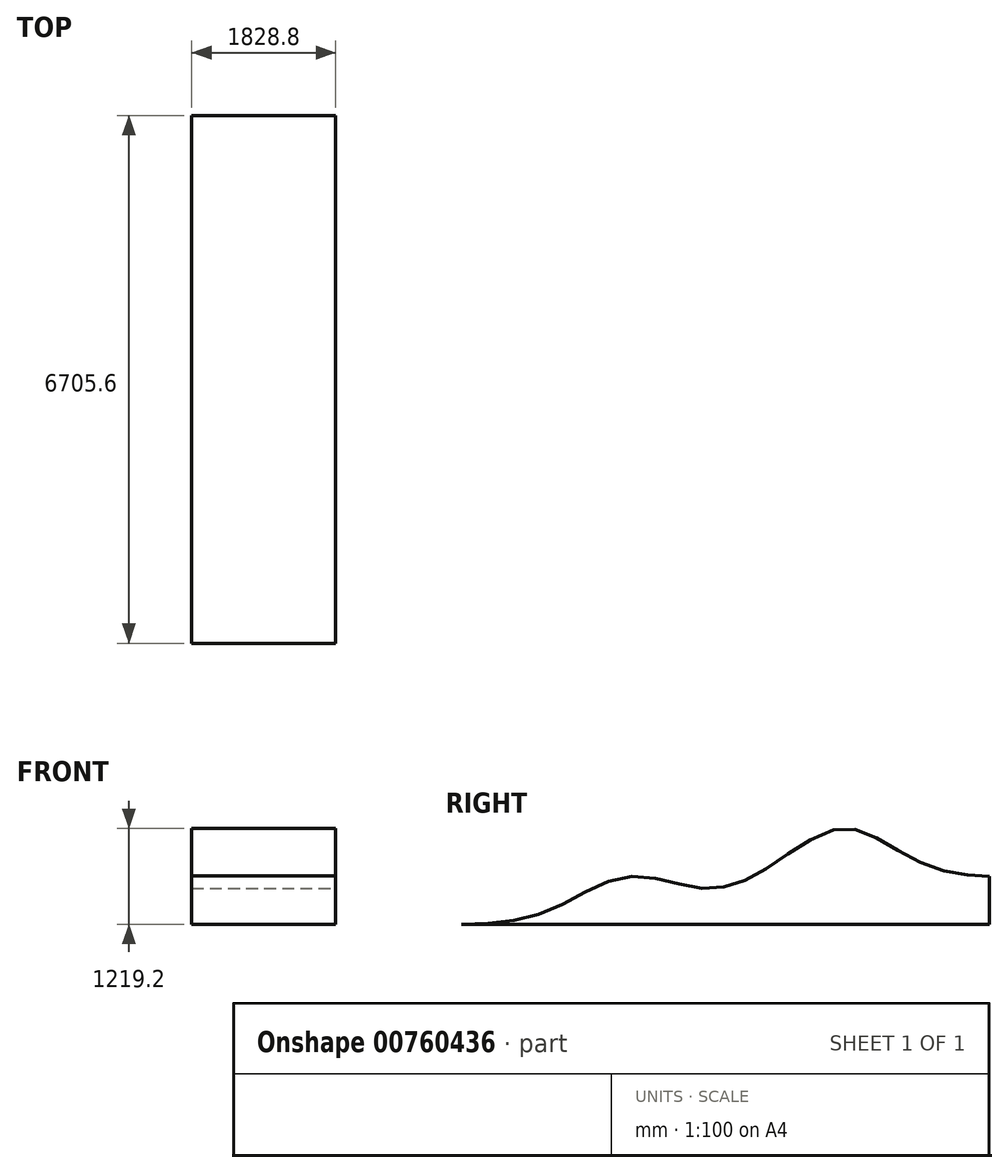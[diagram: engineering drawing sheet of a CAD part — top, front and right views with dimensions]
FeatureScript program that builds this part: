
annotation { "Feature Type Name" : "Feature", "Feature Type Description" : "" }
export const myFeature = defineFeature(function(context is Context, id is Id, definition is map)
    precondition{}
    {
        {
            var Q0;
            Q0=qCreatedBy(makeId("Right.planeOp"),FACE);
            var sketch = newSketch(context, id + "F0", { "sketchPlane" : qUnion([Q0])});
            skLineSegment(sketch, "E0", {"start": v(-1124.07, -3108.87) * mm, "end": v(5581.53, -3108.87) * mm});
            skFitSpline(sketch, "E1", {"points": [v(-1124.07, -3108.87) * mm, v(0, -2924.97) * mm, v(1009.53, -2499.27) * mm, v(1962.31, -2651.67) * mm, v(2786.78, -2373.01) * mm, v(3752.73, -1889.67) * mm, v(4640.5, -2295.62) * mm, v(5581.53, -2499.27) * mm], "startDerivative": vector(7863.79, 0) * mm, "endDerivative": vector(6120.43, 3.5) * mm});
            skLineSegment(sketch, "E2", {"start": v(5581.53, -2499.27) * mm, "end": v(5581.53, -3108.87) * mm});
            skSolve(sketch);
        }
        {
            var Q0;
            Q0 = qSketchRegion(id + "F0", true);
            extrude(context, id + "F1", {"entities" : qUnion([Q0]), "depth" : 1828.8 * mm, "offsetDistance" : 30.48 * mm});
        }
    });
